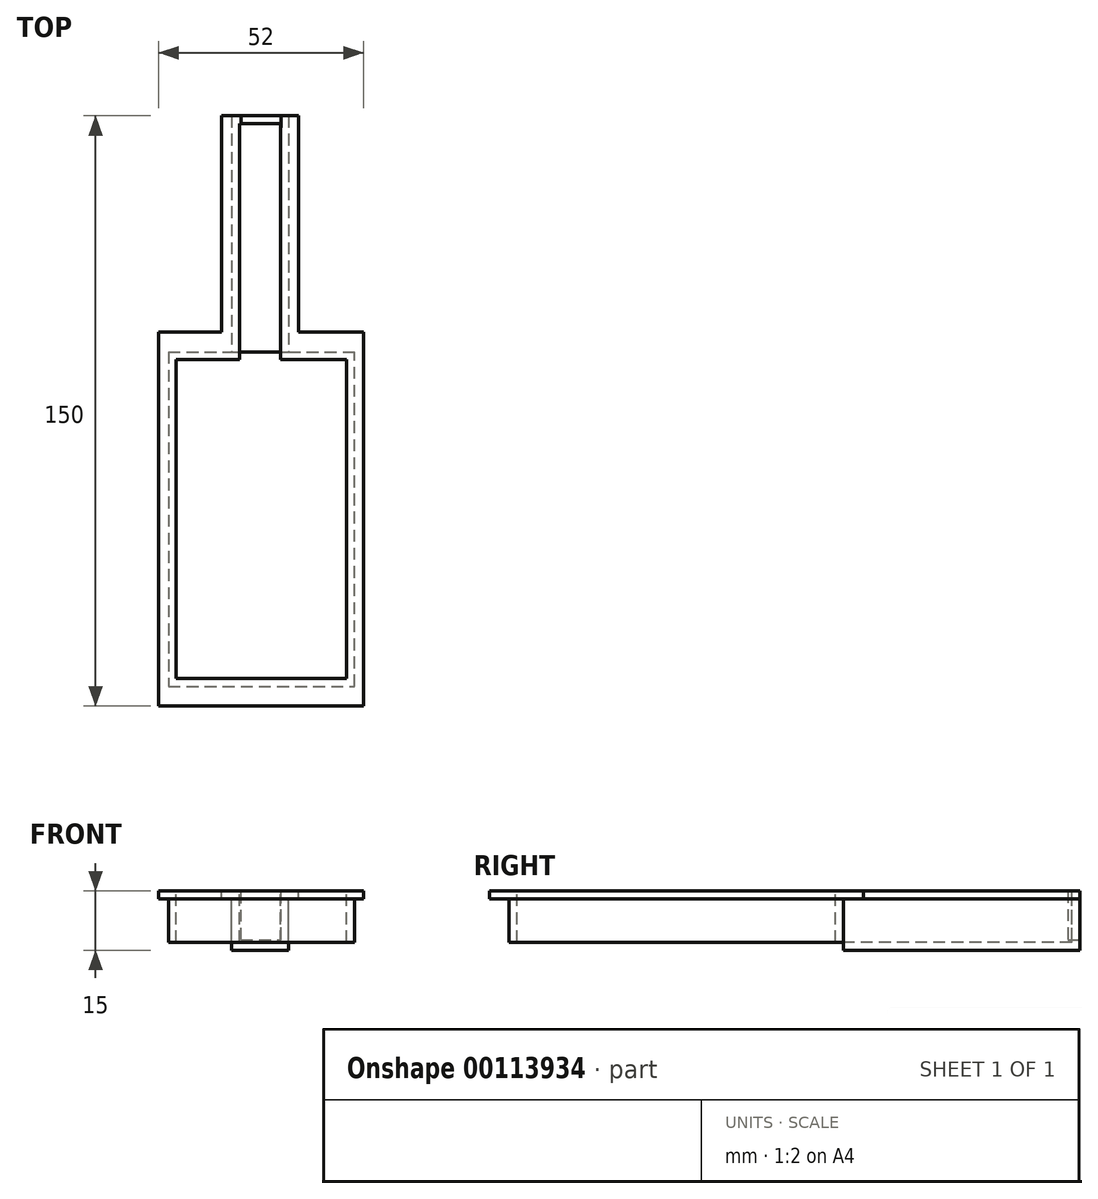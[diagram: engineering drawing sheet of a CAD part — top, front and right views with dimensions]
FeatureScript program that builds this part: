
annotation { "Feature Type Name" : "Feature", "Feature Type Description" : "" }
export const myFeature = defineFeature(function(context is Context, id is Id, definition is map)
    precondition{}
    {
        {
            var Q0;
            Q0=qCreatedBy(makeId("Top.planeOp"),FACE);
            var sketch = newSketch(context, id + "F0", { "sketchPlane" : qUnion([Q0])});
            skPoint(sketch, "E0.middle", {"position": v(0, 0) * mm});
            skLineSegment(sketch, "E1.1", {"start": v(26, -75) * mm, "end": v(26, 20) * mm});
            skLineSegment(sketch, "E1.2", {"start": v(26, -75) * mm, "end": v(-26, -75) * mm});
            skLineSegment(sketch, "E1.3", {"start": v(-26, -75) * mm, "end": v(-26, 20) * mm});
            skPoint(sketch, "E2.orphan", {"position": v(-21, 70) * mm});
            skPoint(sketch, "E3.orphan", {"position": v(21, 70) * mm});
            skLineSegment(sketch, "E4", {"start": v(-26, 20) * mm, "end": v(-10, 20) * mm});
            skLineSegment(sketch, "E5.trimOffspring", {"start": v(9.5, 20) * mm, "end": v(26, 20) * mm});
            skPoint(sketch, "E6.orphan", {"position": v(-5, 15) * mm});
            skPoint(sketch, "E7.orphan", {"position": v(4.5, 15) * mm});
            skLineSegment(sketch, "E8", {"start": v(-10, 20) * mm, "end": v(-10, 75) * mm});
            skLineSegment(sketch, "E9", {"start": v(9.5, 20) * mm, "end": v(9.5, 75) * mm});
            skPoint(sketch, "E10.orphan", {"position": v(0, 70) * mm});
            skPoint(sketch, "E11.end.orphan", {"position": v(-5, 75) * mm});
            skPoint(sketch, "E12.end.orphan", {"position": v(4.5, 75) * mm});
            skPoint(sketch, "E13.orphan", {"position": v(0, -70) * mm});
            skPoint(sketch, "E14.orphan", {"position": v(-5, 70) * mm});
            skPoint(sketch, "E0.top.start.orphan", {"position": v(4.5, 70) * mm});
            skPoint(sketch, "E15.orphan", {"position": v(-21, -70) * mm});
            skPoint(sketch, "E0.bottom.start.orphan", {"position": v(21, -70) * mm});
            skLineSegment(sketch, "E16", {"start": v(9.5, 75) * mm, "end": v(4.5, 75) * mm});
            skLineSegment(sketch, "E17.0", {"start": v(21, -70) * mm, "end": v(-21, -70) * mm});
            skLineSegment(sketch, "E17.3", {"start": v(7, 15) * mm, "end": v(21, 15) * mm});
            skLineSegment(sketch, "E18.trimOffspring", {"start": v(-5, 75) * mm, "end": v(-10, 75) * mm});
            skLineSegment(sketch, "E19", {"start": v(-7.5, 75) * mm, "end": v(-7.5, 15) * mm});
            skLineSegment(sketch, "E20", {"start": v(7, 75) * mm, "end": v(7, 15) * mm});
            skLineSegment(sketch, "E21", {"start": v(-23.52, 15) * mm, "end": v(-23.52, -70) * mm});
            skLineSegment(sketch, "E22", {"start": v(-23.52, -70) * mm, "end": v(23.79, -70) * mm});
            skLineSegment(sketch, "E23", {"start": v(23.79, -70) * mm, "end": v(23.79, 15) * mm});
            skLineSegment(sketch, "E24", {"start": v(23.79, 15) * mm, "end": v(21, 15) * mm});
            skLineSegment(sketch, "E25", {"start": v(-5, 75) * mm, "end": v(7, 75) * mm});
            skPoint(sketch, "E17.4.start.orphan", {"position": v(-21, 15) * mm});
            skLineSegment(sketch, "E26", {"start": v(-23.52, 15) * mm, "end": v(-7.5, 15) * mm});
            skSolve(sketch);
        }
        {
            var Q0;
            Q0=makeQuery(id+"F0.imprint","IMPRINT",FACE,{"disambiguationData":[TD([[makeQuery(id+"F0.imprint","IMPRINT",EDGE,{"derivedFrom":sQuery(id+"F0.wireOp",EDGE,"E17.3")}),-1.0]])]});
            extrude(context, id + "F1", {"entities" : qUnion([Q0]), "oppositeDirection" : true, "depth" : 15 * mm});
        }
        {
            var Q0;
            Q0=makeQuery(id+"F1.opExtrude","CAP_FACE",FACE,{"disambiguationData":[OSD([sQuery(id+"F0.wireOp",EDGE,"E17.3"),sQuery(id+"F0.wireOp",EDGE,"E18.trimOffspring"),sQuery(id+"F0.wireOp",EDGE,"E19"),sQuery(id+"F0.wireOp",EDGE,"E20"),sQuery(id+"F0.wireOp",EDGE,"E21"),sQuery(id+"F0.wireOp",EDGE,"E22"),sQuery(id+"F0.wireOp",EDGE,"E23"),sQuery(id+"F0.wireOp",EDGE,"E24"),sQuery(id+"F0.wireOp",EDGE,"E25"),sQuery(id+"F0.wireOp",EDGE,"E26")])],"isStart":true});
            shell(context, id + "F2", {"entities" : qUnion([Q0]), "thickness" : 2 * mm});
        }
        {
            var Q0;
            Q0=makeQuery(id+"F0.imprint","IMPRINT",FACE,{"disambiguationData":[TD([[makeQuery(id+"F0.imprint","IMPRINT",EDGE,{"derivedFrom":sQuery(id+"F0.wireOp",EDGE,"E1.1")}),1.0]])]});
            extrude(context, id + "F3", {"entities" : qUnion([Q0]), "operationType" : NewBodyOperationType.ADD, "oppositeDirection" : true, "depth" : 2 * mm});
        }
        {
            var Q0;
            Q0=makeQuery(id+"F1.opExtrude","CAP_FACE",FACE,{"disambiguationData":[OSD([sQuery(id+"F0.wireOp",EDGE,"E17.3"),sQuery(id+"F0.wireOp",EDGE,"E18.trimOffspring"),sQuery(id+"F0.wireOp",EDGE,"E19"),sQuery(id+"F0.wireOp",EDGE,"E20"),sQuery(id+"F0.wireOp",EDGE,"E21"),sQuery(id+"F0.wireOp",EDGE,"E22"),sQuery(id+"F0.wireOp",EDGE,"E23"),sQuery(id+"F0.wireOp",EDGE,"E24"),sQuery(id+"F0.wireOp",EDGE,"E25"),sQuery(id+"F0.wireOp",EDGE,"E26")])],"isStart":false});
            var sketch = newSketch(context, id + "F4", { "sketchPlane" : qUnion([Q0])});
            skLineSegment(sketch, "E27.bottom", {"start": v(-23.52, 70) * mm, "end": v(23.79, 70) * mm});
            skLineSegment(sketch, "E27.top", {"start": v(-23.52, -15) * mm, "end": v(23.79, -15) * mm});
            skLineSegment(sketch, "E27.left", {"start": v(-23.52, 70) * mm, "end": v(-23.52, -15) * mm});
            skLineSegment(sketch, "E27.right", {"start": v(23.79, 70) * mm, "end": v(23.79, -15) * mm});
            skSolve(sketch);
        }
        {
            var Q0;
            Q0=makeQuery(id+"F4.imprint","IMPRINT",FACE,{"disambiguationData":[TD([[makeQuery(id+"F4.imprint","IMPRINT",EDGE,{"derivedFrom":sQuery(id+"F4.wireOp",EDGE,"E27.bottom")}),-1.0]])]});
            extrude(context, id + "F5", {"entities" : qUnion([Q0]), "operationType" : NewBodyOperationType.REMOVE, "oppositeDirection" : true, "depth" : 2 * mm});
        }
        {
            var Q0;
            {var subQ0=sQuery(id+"F0.wireOp",EDGE,"E18.trimOffspring");Q0=makeQuery(id+"F3.boolean.opBoolean","MERGE",FACE,{"derivedFrom":[makeQuery(id+"F1.opExtrude","SWEPT_FACE",FACE,{"disambiguationData":[OSD([subQ0,sQuery(id+"F0.wireOp",EDGE,"E25")])]}),makeQuery(id+"F3.opExtrude","SWEPT_FACE",FACE,{"disambiguationData":[OSD([sQuery(id+"F0.wireOp",EDGE,"E16")])]}),makeQuery(id+"F3.opExtrude","SWEPT_FACE",FACE,{"disambiguationData":[OSD([subQ0])]})]});}
            var sketch = newSketch(context, id + "F6", { "sketchPlane" : qUnion([Q0])});
            skLineSegment(sketch, "E28.bottom", {"start": v(5.07, -12.34) * mm, "end": v(-5.07, -12.34) * mm});
            skLineSegment(sketch, "E28.top", {"start": v(5.07, 2.42) * mm, "end": v(-5.07, 2.42) * mm});
            skLineSegment(sketch, "E28.left", {"start": v(5.07, -12.34) * mm, "end": v(5.07, 2.42) * mm});
            skLineSegment(sketch, "E28.right", {"start": v(-5.07, -12.34) * mm, "end": v(-5.07, 2.42) * mm});
            skPoint(sketch, "E28.middle", {"position": v(0, -4.96) * mm});
            skSolve(sketch);
        }
        {
            var Q0;
            {var subQ0=sQuery(id+"F6.wireOp",EDGE,"E28.bottom");Q0=makeQuery(id+"F6.imprint","IMPRINT",FACE,{"disambiguationData":[TD([[makeQuery(id+"F6.imprint","IMPRINT",EDGE,{"derivedFrom":subQ0}),-1.0]])]});}
            extrude(context, id + "F7", {"entities" : qUnion([Q0]), "operationType" : NewBodyOperationType.REMOVE, "oppositeDirection" : true, "depth" : 3 * mm});
        }
    });
